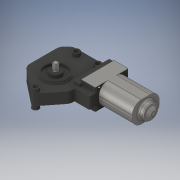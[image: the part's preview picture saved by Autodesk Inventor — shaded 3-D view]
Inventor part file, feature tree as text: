
AUTODESK INVENTOR PART (.ipt)
format: ipt  version: 2019 (Build 230136000, 136)  size: 735,232 bytes
history: native  units: mm
features: sketch x22, extrude x18, fillet x11, projected_geometry x7, other x6, mirror x4, loft x1, chamfer x1
ambient origin geometry x8: Origin, YZ Plane, XZ Plane, XY Plane, X Axis, Y Axis, Z Axis, Center Point
bodies: Body1 (feature_tree)
feature tree (70):
  other  "Твердое тело1"
  extrude  "Выдавливание1"  Depth=50.6mm
  extrude  "Выдавливание2"  Depth=63.0mm
  sketch  "Эскиз3"
  other  "РабПлоскость1"
  loft  "Лофт1"
  fillet  "Сопряжение1"  Radius=28.3mm
  fillet  "Сопряжение2"  Radius=19.75mm
  fillet  "Сопряжение3"  Radius=25.3mm
  fillet  "Сопряжение4"  Radius=10.0mm
  extrude  "Выдавливание3"  Depth=20.0mm
  extrude  "Выдавливание4"  Depth=5.0mm
  extrude  "Выдавливание5"  Depth=8.0mm
  other  "РабПлоскость2"
  mirror  "Зеркальное отражение1"
  fillet  "Сопряжение5"  [1 undecoded]
  extrude  "Выдавливание6"  TaperAngle=0.0deg  [1 undecoded]
  extrude  "Выдавливание7"  Depth=3.0mm
  fillet  "Сопряжение6"  Radius=1.75mm
  fillet  "Сопряжение7"  Radius=1.75mm
  other  "РабПлоскость3"
  mirror  "Зеркальное отражение2"
  fillet  "Сопряжение8"  Radius=17.0mm
  extrude  "Выдавливание8"  Depth=15.0mm TaperAngle=0.0deg
  extrude  "Выдавливание9"  Depth=37.0mm
  fillet  "Сопряжение9"  Radius=73.5mm
  extrude  "Выдавливание10"  Depth=5.0mm
  extrude  "Выдавливание11"  Depth=39.5mm TaperAngle=0.0deg
  extrude  "Выдавливание12"  Depth=11.0mm
  extrude  "Выдавливание13"  Depth=9.0mm TaperAngle=0.0deg
  sketch  "Эскиз16"
  extrude  "Выдавливание14"  Depth=1.75mm
  fillet  "Сопряжение10"  Radius=13.4mm
  chamfer  "Фаска1"  Distance=67.0mm
  fillet  "Сопряжение11"  Radius=6.4mm
  sketch  "Эскиз18"
  extrude  "Выдавливание15"  Depth=9.0mm
  mirror  "Зеркальное отражение3"
  extrude  "Выдавливание16"  Depth=2.9mm TaperAngle=0.0deg
  extrude  "Выдавливание17"  Depth=2.75mm
  other  "РабПлоскость4"
  mirror  "Зеркальное отражение4"
  other  "РабПлоскость5"
  extrude  "Выдавливание19"  Depth=1.0mm
  sketch  "Эскиз1"
  sketch  "Эскиз2"
  sketch  "Эскиз4"
  sketch  "Эскиз5"
  projected_geometry  "Спроецированная петля1"
  sketch  "Эскиз6"
  sketch  "Эскиз7"
  sketch  "Эскиз8"
  sketch  "Эскиз9"
  projected_geometry  "Спроецированная петля2"
  sketch  "Эскиз10"
  sketch  "Эскиз11"
  sketch  "Эскиз12"
  projected_geometry  "Спроецированная петля3"
  projected_geometry  "Спроецированная петля4"
  sketch  "Эскиз13"
  sketch  "Эскиз14"
  sketch  "Эскиз15"
  sketch  "Эскиз17"
  sketch  "Эскиз19"
  projected_geometry  "Спроецированная петля6"
  sketch  "Эскиз20"
  projected_geometry  "Спроецированная петля7"
  sketch  "Эскиз21"
  projected_geometry  "Спроецированная петля8"
  sketch  "Эскиз23"
note: 2 required parameter values undecoded (feature->parameter linkage not recoverable at this tier; creation-order binding heuristic only, values carry confidence <= 0.55)
